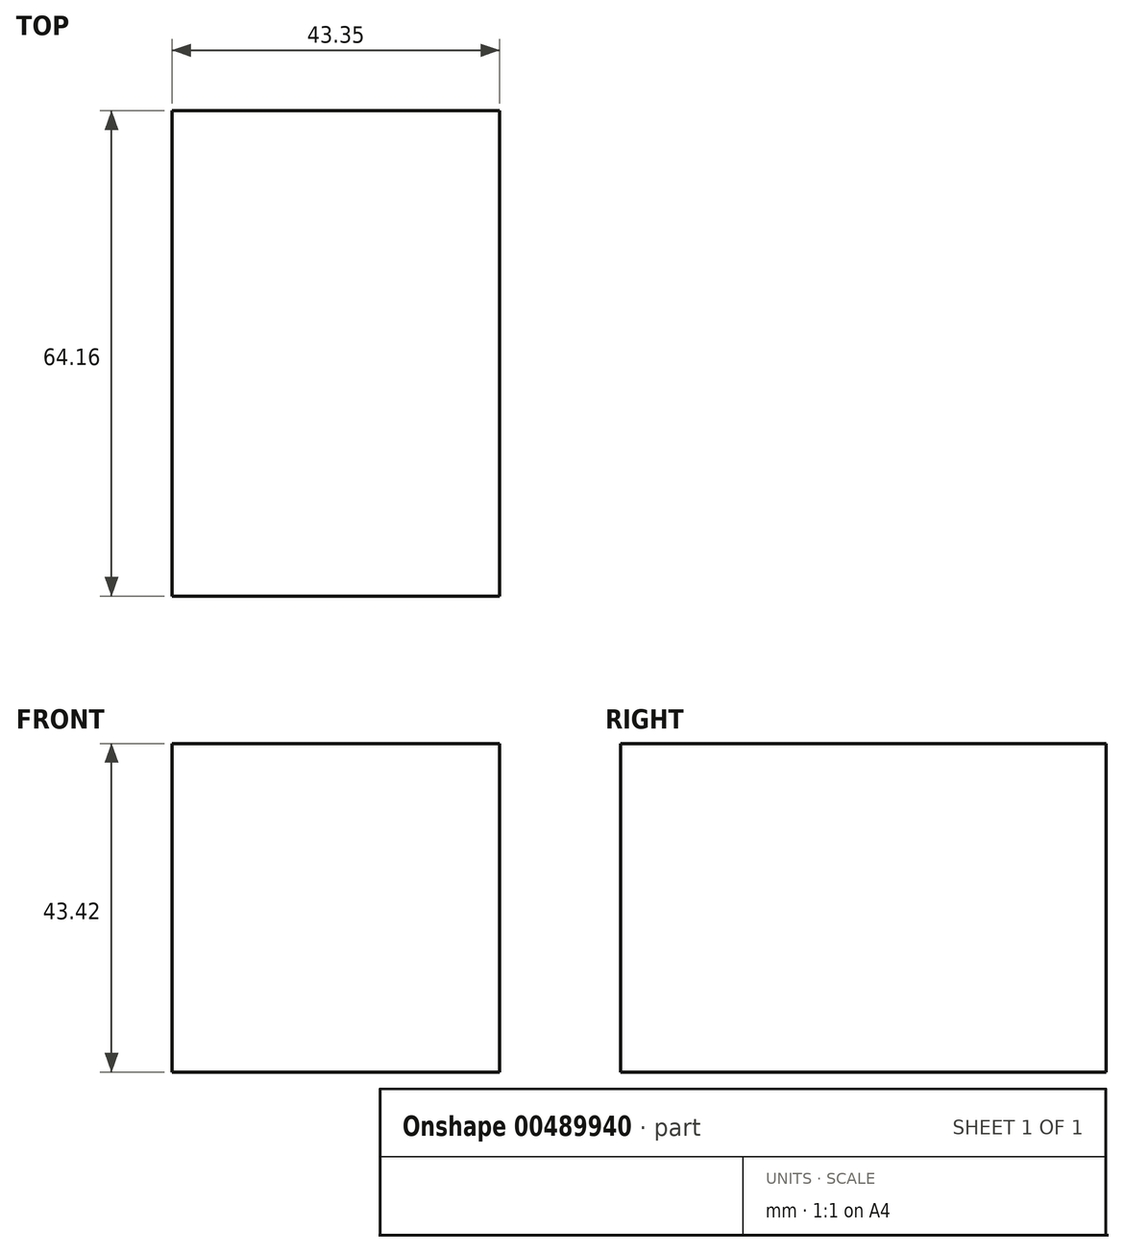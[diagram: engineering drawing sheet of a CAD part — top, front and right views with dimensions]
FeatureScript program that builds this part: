
annotation { "Feature Type Name" : "Feature", "Feature Type Description" : "" }
export const myFeature = defineFeature(function(context is Context, id is Id, definition is map)
    precondition{}
    {
        {
            var Q0;
            Q0=qCreatedBy(makeId("Front.planeOp"),FACE);
            var sketch = newSketch(context, id + "F0", { "sketchPlane" : qUnion([Q0])});
            skLineSegment(sketch, "E0.bottom", {"start": v(18.45, 28.32) * mm, "end": v(61.8, 28.32) * mm});
            skLineSegment(sketch, "E0.top", {"start": v(18.45, 71.74) * mm, "end": v(61.8, 71.74) * mm});
            skLineSegment(sketch, "E0.left", {"start": v(18.45, 28.32) * mm, "end": v(18.45, 71.74) * mm});
            skLineSegment(sketch, "E0.right", {"start": v(61.8, 28.32) * mm, "end": v(61.8, 71.74) * mm});
            skSolve(sketch);
        }
        {
            var Q0;
            Q0 = qSketchRegion(id + "F0", true);
            extrude(context, id + "F1", {"entities" : qUnion([Q0]), "depth" : 64.16 * mm});
        }
    });
